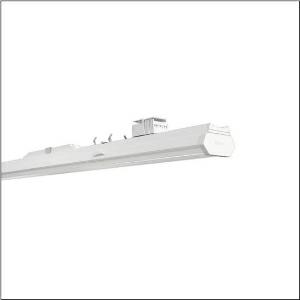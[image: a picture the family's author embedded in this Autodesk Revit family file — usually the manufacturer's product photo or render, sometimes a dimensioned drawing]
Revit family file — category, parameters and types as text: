
# Revit family: licross_r__11_protected_mo_51td12dn495g_4259
name_source: partatom
category: Lighting Fixtures
units: mm (PartAtom-declared; Revit-internal decimal feet)

## family parameters
Cut with Voids When Loaded = No
Host = Face
Light Source = No
Part Type = Normal
Room Calculation Point = No
Round Connector Dimension = Use Diameter
Shared = No

## types (1)
- --- (1 x LED, 9980 lm, 57.1 W, 4000K)
    Apparent Load = 57 VA
    CIE Flux Codes = 73 92 98 99 100
    Color Rendering = 80
    Color Temperature = 4000K
    Default Elevation = 1800 mm
    Description = Licross® 11 Protected MO, luminaire insert, of sheet steel, galvanised, coil coated, white, length: 1.500mm, width: 90mm, height: 101mm, LED rated luminous flux: 9.980lm, light colour: 840, control gear: DALI 2, control gear: ECG DALI, with plug, 5-pole, with phase selection, mains connection: 220..240V, AC, 50/60Hz, halogen-free wiring, primary optical cover: cover, of PMMA, light emission: direct with ceiling illumination distribution, primary light characteristic: symmetric, protection rating (complete): IP54, insulation class (complete): insulation class I (protective earthing), certification: CE, ENEC, VDE, UKCA, protection symbol: D if used in an environment with non-conductive dust loads with corresponding accessories, impact resistance: IK06, permissible ambient temperature for indoor applications: -25..+35°C, corresponds to IFS (International Featured Standards) requirements for safety and quality in the food industry, reducing of maximum allowable ambient temperature of 5°C with ceiling mounting, LABS conformity tested according to VDMA 24364:2018-05, packaging unit: 1 piece
    Height = 92 mm
    Lamp = 1 x LED
    Lamp Light Flux = 9980 lm
    Lamp Power = 57.1 W
    Lamp count = 1
    Length = 1500 mm
    Luminous efficacy = 175 lm/W
    Manufacturer = Siteco
    ModVariant = No
    Model = 51TD12DN495G
    Mounting Place = Ceiling
    Mounting Type = Pendant
    Number of Poles = 1
    OnlyDefault = Yes
    Power Factor = 1
    Product Name = Licross® 11 Protected MO
    Product group = luminaire insert
    ProductGroupID = 902
    Protection Class = Protection class I
    Protection Degree = IP 54
    RLX_Detail_Level = 1
    RlxData = <blob elided: 24381 chars, md5=a9b2fd05>
    Socket = socket
    Standby Power = 0 W
    System Light Flux = 9980 lm
    System Power = 57 W
    Type Comments = factory setting: luminous flux: 100 % | dim-lin: 254 | 378 mA
    Type Image = l_1256145.jpg
    URL = http://relux.com
    VarID = @adj_010291
    Voltage = 0 V
    Weight = 0.00 kg
    Width = 88 mm

## geometry (parser evidence)
native form markers: Blend x4, Sweep x12
no freeform markers — native parametric forms only
